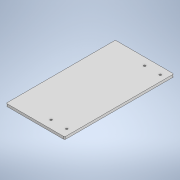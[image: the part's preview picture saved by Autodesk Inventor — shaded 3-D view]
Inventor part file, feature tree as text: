
AUTODESK INVENTOR PART (.ipt)
format: ipt  version: 2021 (Build 250183000, 183)  size: 117,248 bytes
history: native  units: mm
features: sketch x2, extrude x1, fillet x1, hole x1
ambient origin geometry x8: Origin, YZ Plane, XZ Plane, XY Plane, X Axis, Y Axis, Z Axis, Center Point
bodies: Solid1 (feature_tree)
feature tree (5):
  extrude  "Extrusion1"  Depth=217.0mm
  fillet  "Fillet1"  Radius=217.0mm
  hole  "Hole1"  [1 undecoded]
  sketch  "Sketch1"  dims[d4=5.0mm d5=111.2mm d6=217.0mm]
  sketch  "Sketch2"  dims[d7=217.0mm d8=5.0mm d9=0.0mm d10=2.0mm d12=186.0mm d13=4.0mm d14=6.0mm d15=4.0mm d16=2.0mm d17=90.0deg d18=8.0mm d19=20.594885mm d20=12.0mm d21=31.0mm]
note: 1 required parameter value undecoded (feature->parameter linkage not recoverable at this tier; creation-order binding heuristic only, values carry confidence <= 0.55)
